# Revit family: Mascali Round UL - folded
name_source: partatom
category: Lighting Fixtures
units: mm (PartAtom-declared; Revit-internal decimal feet)

## family parameters
Always vertical = Yes
Cut with Voids When Loaded = No
Host = Wall
Light Source = Yes
OmniClass Number = 23.80.70.00
OmniClass Title = Lighting
Part Type = Normal
Room Calculation Point = No
Round Connector Dimension = Use Diameter
Shared = No

## types (2) — shared parameters
Color Filter = 16777215
Dimming Lamp Color Temperature Shift = <None>
Driver Required = No
Main Material = Metal - Steel
Manufacturer = Astro Lighting Ltd
Product Location = Bathroom
URL = www.astrolighting.com
zero-valued in all types: Default Elevation

## per-type parameters (varying)
| type | ADA compliant | Apparent Load | Dimmable | Dimming Method | Driver Included | Efficacy (lm/w) | Electrical Class | Lamp | Length of Cable Supplied | Light Source Fixed | Location rating | Main Finish | Photometric Web File | Power (Watts) | Product Code | Product Name | Product SKU | Tilt Angle | Wattage Comments |
| CE | Yes - if installed in compliance with ADA §307.2, 308, 309.3, 309.4 | 16 VA | No | Not Applicable | Yes (integral) | 19 | 1 | LED | Not Applicable | Yes | Not applicable | Various | 1373014_Mascali Round LED_Photometry_IES_Iss.01.ies | 7.3 | 1373014 | Mascali Round LED | 1373014 | 0.00° | Not Applicable |
| ETL | NO | 0 VA |  |  |  |  | 0 |  |  |  | DAMP |  | generic |  | 1234 |  | 1234001 | 60.00° |  |

## geometry (parser evidence)
native form markers: Sweep x3
no freeform markers — native parametric forms only
